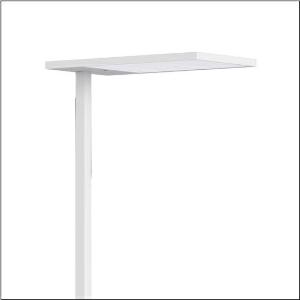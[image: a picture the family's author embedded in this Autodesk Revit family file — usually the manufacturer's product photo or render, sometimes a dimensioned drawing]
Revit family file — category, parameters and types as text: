
# Revit family: silica_r__21_floor_r_51mx53sg4dw_45fa
name_source: partatom
category: Lighting Fixtures
units: mm (PartAtom-declared; Revit-internal decimal feet)

## family parameters
Cut with Voids When Loaded = No
Host = Face
Light Source = No
Part Type = Normal
Room Calculation Point = No
Round Connector Dimension = Use Diameter
Shared = No

## types (1)
- Silica® 21 Floor R (1 x LED, 15000 lm, 106.4 W, 4000K)
    Apparent Load = 106 VA
    CIE Flux Codes = 54 86 97 13 100
    Color Rendering = 80
    Color Temperature = 4000K
    Default Elevation = 1800 mm
    Description = Silica® 21 Floor R, floorstanding luminaire, of PMMA, primary optical cover: prismatic diffuser, of PMMA, CAT 2 (L<= 3000cd/m²), light emission: indirect/direct distribution, primary light characteristic: symmetric, installation type: not mounted, LED, rated luminous flux: 15.000lm, luminous efficacy: 141lm/W, light colour: 840, colour temperature: 4000K, control gear: ECG DALI, daylight-dependent control, mains connection: 230V, 50Hz, connection cable pre-assembled, cable length: 2,5m, rated input power: 106.4W, luminaire head, of aluminium, traffic white (RAL 9016), length: 650mm, width: 350mm, supporting column, angular, of aluminium, traffic white (RAL 9016), baseplate, of steel, traffic white (RAL 9016), protection rating (complete): IP20, insulation class (complete): insulation class I (protective earthing), certification: CE, standard: EN 50419, packaging unit: 1 piece
    Height = 18 mm
    Lamp = 1 x LED
    Lamp Light Flux = 15000 lm
    Lamp Power = 106.4 W
    Lamp count = 1
    Length = 650 mm
    Luminous efficacy = 141 lm/W
    Manufacturer = Siteco
    ModVariant = No
    Model = 51MX53SG4DW
    Mounting Place = Floor
    Mounting Type = Freestanding
    Number of Poles = 1
    OnlyDefault = Yes
    Power Factor = 1
    Product Name = Silica® 21 Floor R
    Product group = floorstanding luminaire
    ProductGroupID = 1301
    Protection Class = Protection class I
    Protection Degree = IP 20
    RLX_Detail_Level = 1
    RLX_Emergency_Light_Flux = 0 lm
    RLX_Emergency_Type = 0
    RLX_Emergency_Type_DB = No
    RlxData = <blob elided: 18625 chars, md5=65518889>
    Socket = socket
    Standby Power = 0 W
    System Light Flux = 15000 lm
    System Power = 106 W
    Type Comments = Product without accessories
    Type Image = l_1003935.jpg
    URL = http://relux.com
    VarID = ---
    Voltage = 0 V
    Weight = 0.00 kg
    Width = 350 mm

## geometry (parser evidence)
native form markers: Blend x4, Sweep x15
no freeform markers — native parametric forms only
